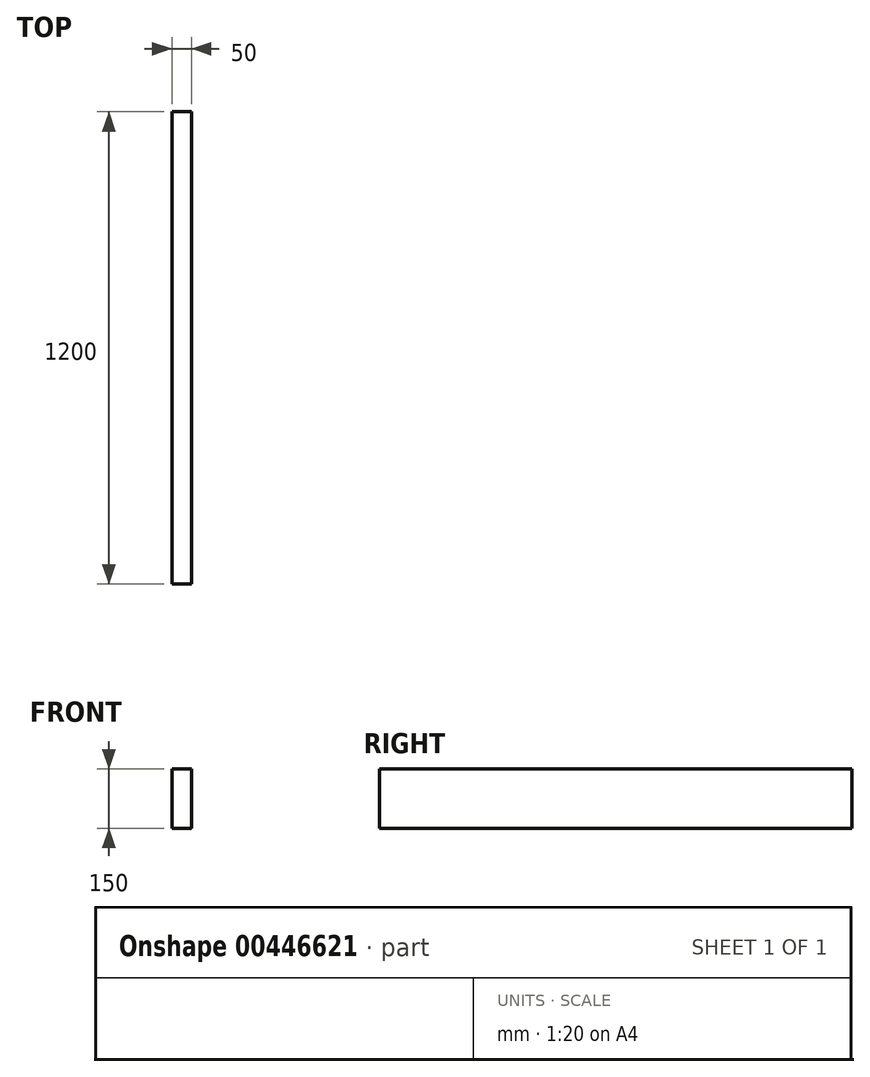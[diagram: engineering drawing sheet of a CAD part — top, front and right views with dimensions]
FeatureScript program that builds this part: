
annotation { "Feature Type Name" : "Feature", "Feature Type Description" : "" }
export const myFeature = defineFeature(function(context is Context, id is Id, definition is map)
    precondition{}
    {
        {
            var Q0;
            Q0=qCreatedBy(makeId("Front.planeOp"),FACE);
            var sketch = newSketch(context, id + "F0", { "sketchPlane" : qUnion([Q0])});
            skLineSegment(sketch, "E0.bottom", {"start": v(25, -75) * mm, "end": v(-25, -75) * mm});
            skLineSegment(sketch, "E0.top", {"start": v(25, 75) * mm, "end": v(-25, 75) * mm});
            skLineSegment(sketch, "E0.left", {"start": v(25, -75) * mm, "end": v(25, 75) * mm});
            skLineSegment(sketch, "E0.right", {"start": v(-25, -75) * mm, "end": v(-25, 75) * mm});
            skPoint(sketch, "E0.middle", {"position": v(0, 0) * mm});
            skSolve(sketch);
        }
        {
            var Q0;
            Q0=makeQuery(id+"F0.imprint","IMPRINT",FACE,{"disambiguationData":[TD([[makeQuery(id+"F0.imprint","IMPRINT",EDGE,{"derivedFrom":sQuery(id+"F0.wireOp",EDGE,"E0.bottom")}),-1.0]])]});
            extrude(context, id + "F1", {"entities" : qUnion([Q0]), "depth" : 1200 * mm});
        }
    });
